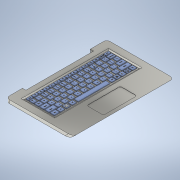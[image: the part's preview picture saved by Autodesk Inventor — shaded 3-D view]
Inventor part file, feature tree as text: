
AUTODESK INVENTOR PART (.ipt)
format: ipt  version: 2022 (Build 260153000, 153)  size: 3,962,880 bytes
history: native  units: mm
features: sketch x14, extrude x14, fillet x4, plane x1, loft x1
ambient origin geometry x8: Origin, YZ Plane, XZ Plane, XY Plane, X Axis, Y Axis, Z Axis, Center Point
bodies: Solid1 (feature_tree)
feature tree (34):
  sketch  "Sketch1"  dims[d0=20.0mm d1=30.0mm]
  plane  "Work Plane1"
  loft  "Loft1"
  extrude  "Extrusion1"  Depth=19.0mm
  fillet  "Fillet1"  Radius=30.0mm
  fillet  "Fillet2"  [1 undecoded]
  extrude  "Extrusion2"  Depth=20.0mm
  fillet  "Fillet3"  Radius=1.0mm
  extrude  "Extrusion3"  Depth=1.0mm TaperAngle=0.0deg
  fillet  "Fillet4"  Radius=1.0mm
  extrude  "Extrusion4"  Depth=5.0mm
  extrude  "Extrusion5"  Depth=10.0mm
  extrude  "Extrusion6"  Depth=0.1mm TaperAngle=0.0deg
  sketch  "Sketch10"  dims[d24=26.0mm d25=2.0mm]
  sketch  "Sketch11"  dims[d26=1.5mm d27=0.25mm d28=0.0mm]
  sketch  "Sketch12"  dims[d29=0.5mm d30=0.75mm]
  sketch  "Sketch13"  dims[d31=1.5mm d32=0.267mm]
  sketch  "Sketch14"  dims[d33=0.25mm d34=150.0mm d36=1.65mm d37=10.0mm d39=10.0mm]
  sketch  "Sketch15"  dims[d41=0.25mm d42=0.0mm d43=1.3mm d44=1.1mm d45=0.25mm d46=0.25mm d47=1.3mm d48=1.4mm d49=1.3mm d50=2.0mm d51=1.3mm d52=2.5mm d53=1.3mm d54=1.6mm d55=0.25mm d56=0.25mm d57=0.25mm d58=0.25mm d59=0.25mm d60=0.25mm d61=0.25mm d62=0.0mm d63=1.3mm d64=1.3mm d65=0.25mm d66=0.5mm d67=120.0mm d69=1.8mm d70=10.0mm d72=10.0mm d74=1.3mm d75=1.667mm d76=0.25mm d77=0.25mm d78=1.3mm d79=1.3mm d80=0.25mm d81=0.25mm d82=130.0mm d84=1.80558mm d85=10.0mm d87=10.0mm d89=1.3mm d90=1.3mm d91=0.25mm d92=0.25mm d93=110.0mm d95=1.85mm d96=10.0mm d98=10.0mm d100=1.3mm d101=2.067mm d102=0.5mm d103=0.25mm d104=1.3mm d105=1.3mm d106=0.25mm d107=0.25mm d108=100.0mm d110=1.9mm d111=10.0mm d113=10.0mm d115=1.3mm d116=2.967mm d117=0.5mm d118=0.25mm d119=1.3mm d120=1.3mm d121=0.25mm d122=0.25mm d123=30.0mm d125=1.75mm d126=10.0mm d128=10.0mm d130=1.3mm d131=1.3mm d132=0.0mm d133=0.25mm d134=0.6mm d135=1.3mm d136=0.6mm d137=1.3mm d138=0.05mm d139=0.0mm d140=0.25mm d141=0.25mm d142=1.3mm d143=1.3mm d144=0.25mm d145=0.25mm d146=1.3mm d147=1.3mm d148=1.3mm d149=1.3mm d150=0.25mm d151=0.25mm d152=0.25mm d153=0.25mm d154=1.3mm d155=9.5mm d156=0.25mm d157=0.4835mm d158=0.2mm d159=0.0mm d160=0.65mm d161=0.9mm d162=0.8mm d163=0.25mm d164=0.2mm d165=0.05mm d166=0.05mm d167=0.3mm d168=0.225mm d169=0.15mm d170=0.460703mm d171=0.043633mm d172=0.5mm d173=0.5mm d174=0.4mm d175=0.4mm d176=0.3mm d177=0.05mm d178=0.025mm d179=0.075mm d180=0.075mm d181=0.075mm d182=0.075mm d183=0.001mm d184=0.0mm d185=0.001mm d186=0.0mm d187=0.001mm d188=0.0mm d189=0.001mm d190=0.0mm d191=0.001mm d192=0.0mm d193=0.001mm d194=0.0mm d195=0.001mm d196=0.0mm d197=0.001mm d198=0.0mm d199=0.0mm d200=0.0mm d201=0.0mm d202=0.0mm]
  extrude  "Extrusion7"  Depth=10.0mm
  extrude  "Extrusion8"  Depth=2.0mm
  extrude  "Extrusion9"  Depth=0.25mm TaperAngle=0.0deg
  extrude  "Extrusion10"  Depth=0.75mm
  extrude  "Extrusion11"  Depth=0.267mm
  extrude  "Extrusion12"  Depth=150.0mm
  extrude  "Extrusion13"  Depth=1.3mm
  extrude  "Extrusion14"  Depth=1.1mm
  sketch  "Sketch2"  dims[d2=-1.0mm d3=19.0mm d4=30.0mm d5=0.0mm d6=90.0deg]
  sketch  "Sketch3"  dims[d7=0.0mm d8=90.0deg d9=20.0mm d10=1.0mm]
  sketch  "Sketch5"  dims[d11=5.0mm d12=1.0mm d13=0.0mm d14=1.0mm]
  sketch  "Sketch6"  dims[d15=0.1mm d16=5.0mm]
  sketch  "Sketch7"  dims[d17=10.0mm d18=10.0mm]
  sketch  "Sketch8"  dims[d19=1.0mm d20=0.1mm d21=0.0mm]
  sketch  "Sketch9"  dims[d22=0.5mm d23=10.0mm]
note: 1 required parameter value undecoded (feature->parameter linkage not recoverable at this tier; creation-order binding heuristic only, values carry confidence <= 0.55)
